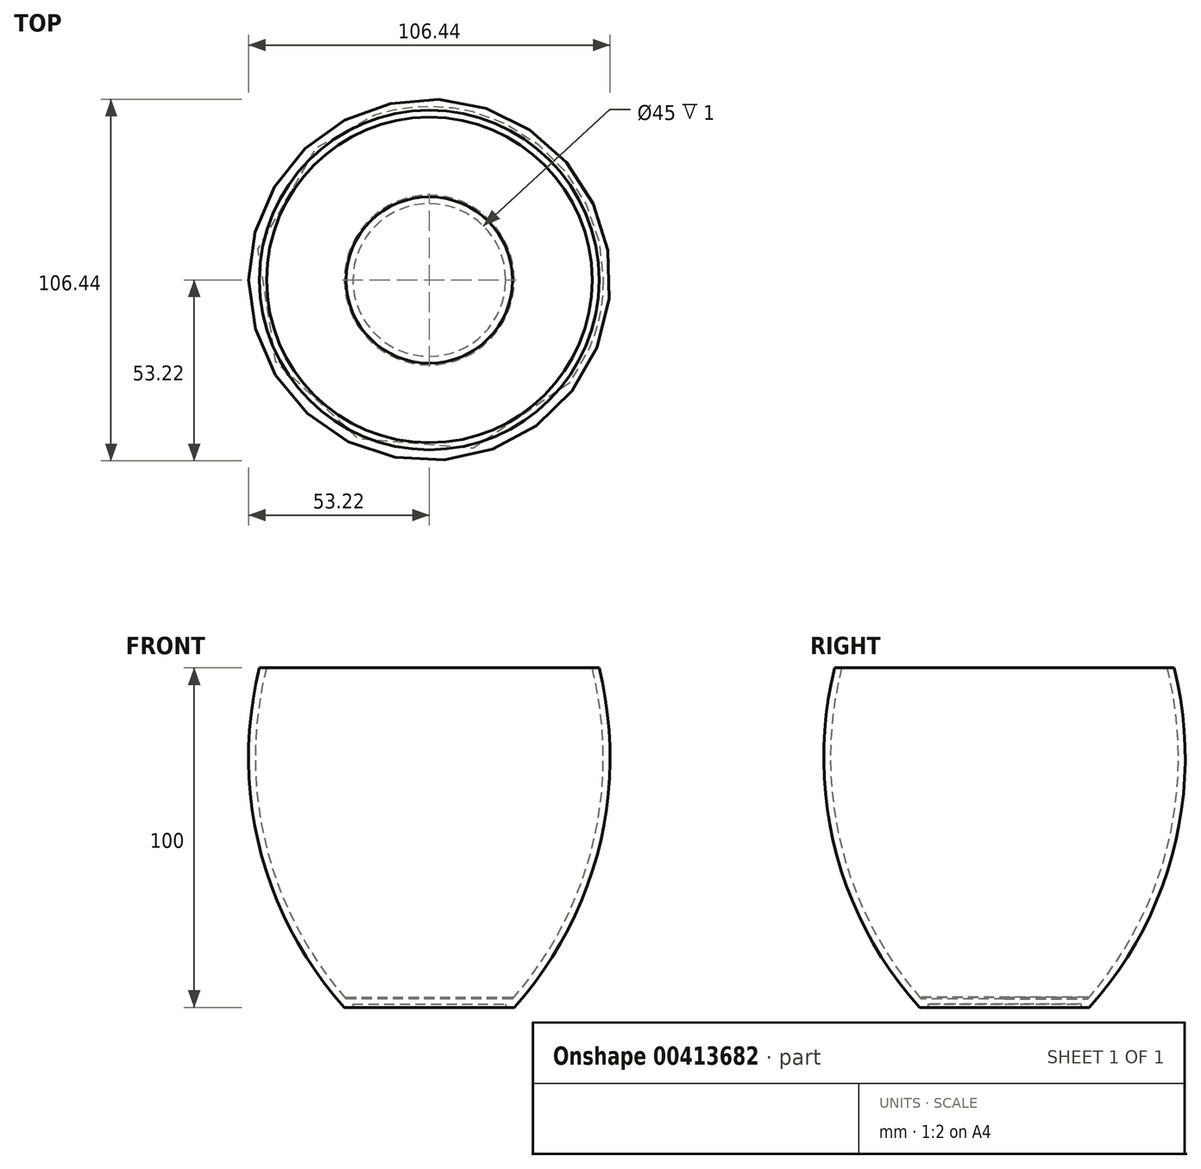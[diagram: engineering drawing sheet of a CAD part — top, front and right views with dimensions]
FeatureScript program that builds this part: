
annotation { "Feature Type Name" : "Feature", "Feature Type Description" : "" }
export const myFeature = defineFeature(function(context is Context, id is Id, definition is map)
    precondition{}
    {
        {
            var Q0;
            Q0=qCreatedBy(makeId("Front.planeOp"),FACE);
            var sketch = newSketch(context, id + "F0", { "sketchPlane" : qUnion([Q0])});
            skLineSegment(sketch, "E0", {"start": v(0, 0) * mm, "end": v(0, 100) * mm});
            skLineSegment(sketch, "E1", {"start": v(0, 0) * mm, "end": v(25, 0) * mm});
            skLineSegment(sketch, "E2", {"start": v(0, 100) * mm, "end": v(50, 100) * mm});
            skArc(sketch, "E3", {"start": v(25, 0) * mm, "mid": v(49.94, 46.9) * mm, "end": v(50, 100) * mm});
            skSolve(sketch);
        }
        {
            var Q0;
            Q0=makeQuery(id+"F0.imprint","IMPRINT",FACE,{"disambiguationData":[TD([[makeQuery(id+"F0.imprint","IMPRINT",EDGE,{"derivedFrom":sQuery(id+"F0.wireOp",EDGE,"E0")}),-1.0]])]});
            var Q1;
            Q1=sQuery(id+"F0.wireOp",EDGE,"E0");
            revolve(context, id + "F1", {"entities" : qUnion([Q0]), "axis" : qUnion([Q1]), "revolveType" : RevolveType.FULL});
        }
        {
            var Q0;
            Q0=makeQuery(id+"F1.opRevolve","SWEPT_FACE",FACE,{"disambiguationData":[OSD([sQuery(id+"F0.wireOp",EDGE,"E1")])]});
            var sketch = newSketch(context, id + "F2", { "sketchPlane" : qUnion([Q0])});
            skCircle(sketch, "E4", {"center": v(0, 0) * mm, "radius": 22.5 * mm});
            skSolve(sketch);
        }
        {
            var Q0;
            Q0 = qSketchRegion(id + "F2", true);
            extrude(context, id + "F3", {"entities" : qUnion([Q0]), "operationType" : NewBodyOperationType.REMOVE, "oppositeDirection" : true, "depth" : 1 * mm});
        }
        {
            var Q0;
            Q0=makeQuery(id+"F1.opRevolve","SWEPT_FACE",FACE,{"disambiguationData":[OSD([sQuery(id+"F0.wireOp",EDGE,"E2")])]});
            shell(context, id + "F4", {"entities" : qUnion([Q0]), "thickness" : 2 * mm});
        }
    });
